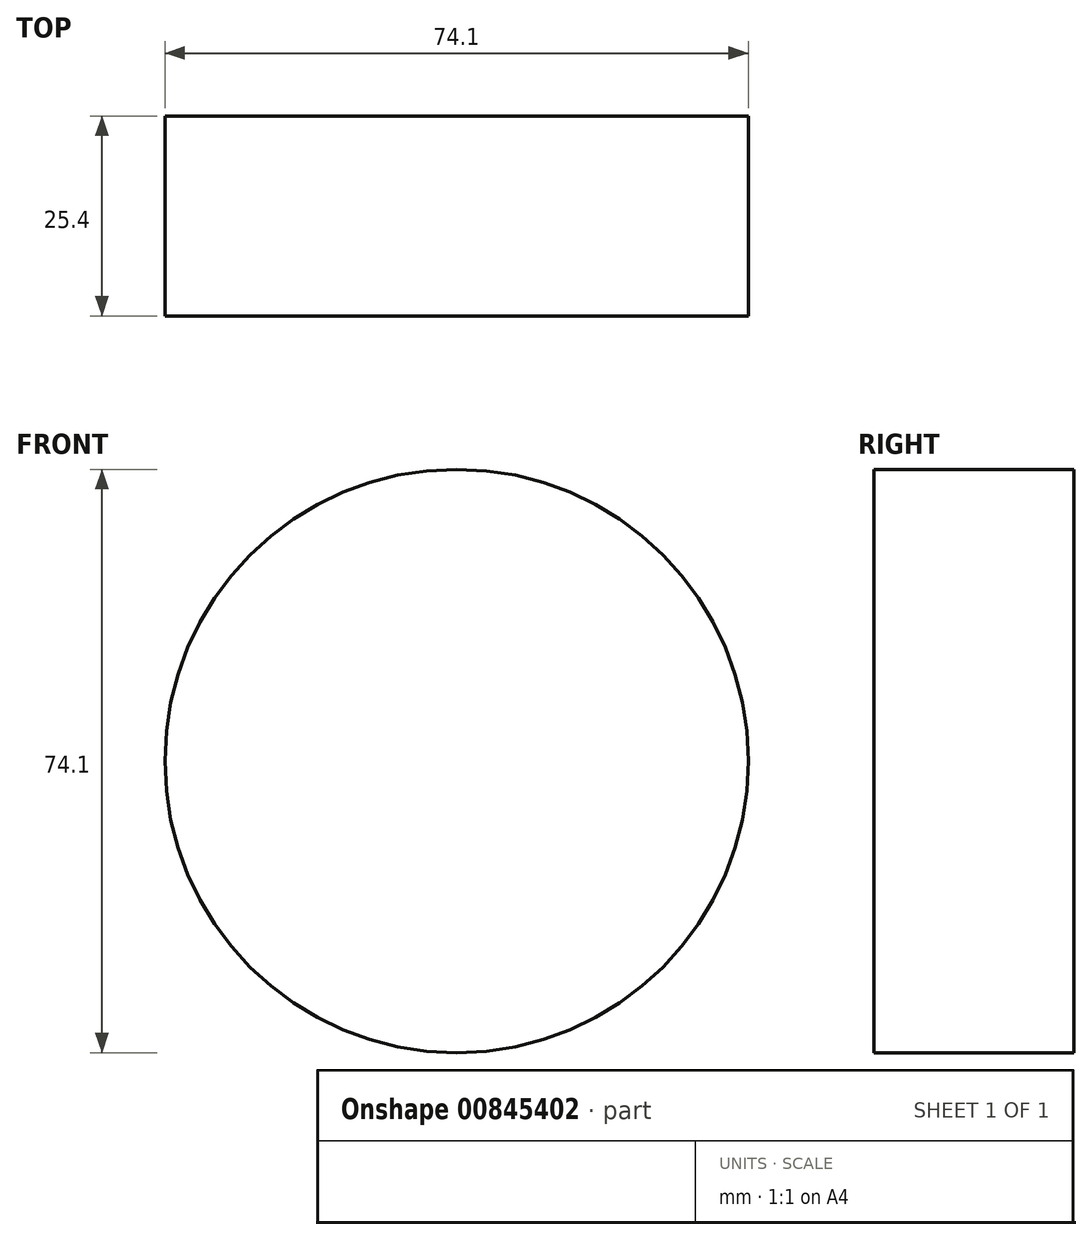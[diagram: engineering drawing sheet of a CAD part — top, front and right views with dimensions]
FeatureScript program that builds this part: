
annotation { "Feature Type Name" : "Feature", "Feature Type Description" : "" }
export const myFeature = defineFeature(function(context is Context, id is Id, definition is map)
    precondition{}
    {
        {
            var Q0;
            Q0=qCreatedBy(makeId("Front.planeOp"),FACE);
            var sketch = newSketch(context, id + "F0", { "sketchPlane" : qUnion([Q0])});
            skCircle(sketch, "E0", {"center": v(0, 0) * mm, "radius": 37.05 * mm});
            skSolve(sketch);
        }
        {
            var Q0;
            Q0=makeQuery(id+"F0.imprint","IMPRINT",FACE,{"disambiguationData":[TD([[makeQuery(id+"F0.imprint","IMPRINT",EDGE,{"derivedFrom":sQuery(id+"F0.wireOp",EDGE,"E0")}),1.0]])]});
            extrude(context, id + "F1", {"entities" : qUnion([Q0]), "depth" : 25.4 * mm, "offsetDistance" : 25.4 * mm});
        }
    });
